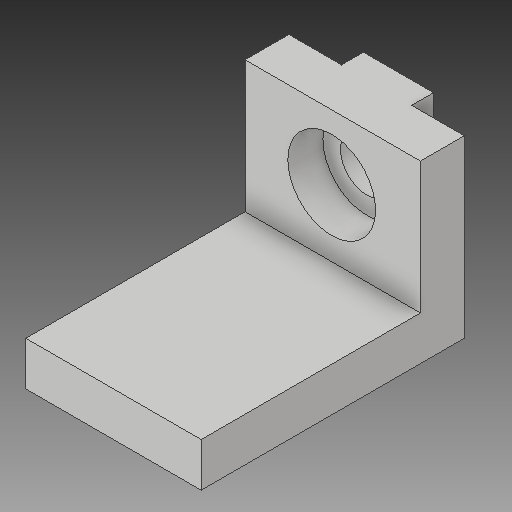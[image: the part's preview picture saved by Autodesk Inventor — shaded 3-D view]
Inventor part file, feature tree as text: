
AUTODESK INVENTOR PART (.ipt)
format: ipt  version: 2019 (Build 230136000, 136)  size: 138,752 bytes
history: native  units: in
note: dims shown in document units (in); Inventor stores cm internally (conversion verified against a paired STEP export)
features: sketch x3, extrude x2, projected_geometry x2, hole x1
ambient origin geometry x8: Origin, YZ Plane, XZ Plane, XY Plane, X Axis, Y Axis, Z Axis, Center Point
bodies: Solid1 (feature_tree)
feature tree (8):
  extrude  "Extrusion1"  Depth=0.5in
  extrude  "Extrusion2"  Depth=0.75in
  hole  "Hole3"  [1 undecoded]
  sketch  "Sketch1"  dims[d0=0.125in d1=0.5in]
  sketch  "Sketch4"  dims[d4=0.125in d5=0.75in]
  projected_geometry  "Projected Loop3"
  sketch  "Sketch5"  dims[d6=0.5in d7=0.0in d22=0.2in d23=0.5in d24=0.15in d25=0.0625in d26=0.0in d27=0.15in d28=0.75in d29=0.25in d30=0.1in d31=0.5635in d32=1.0in d33=0.8108in]
  projected_geometry  "Projected Loop4"
note: 1 required parameter value undecoded (feature->parameter linkage not recoverable at this tier; creation-order binding heuristic only, values carry confidence <= 0.55)
